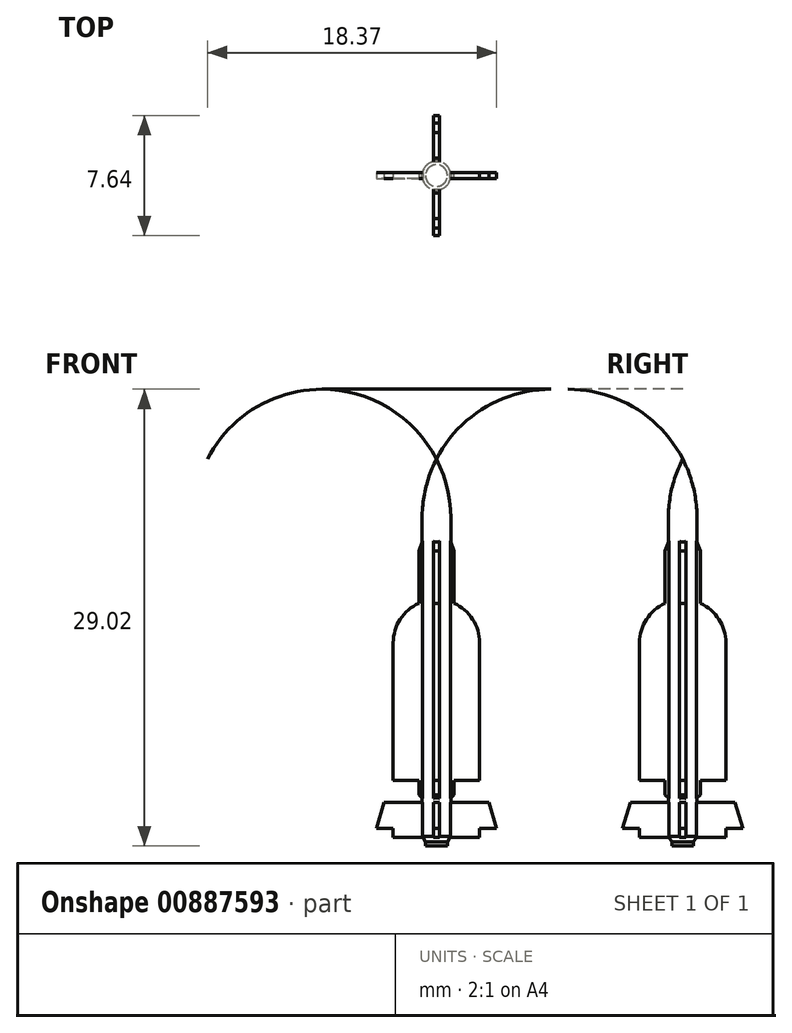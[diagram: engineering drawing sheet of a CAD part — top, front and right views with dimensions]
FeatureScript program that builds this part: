
annotation { "Feature Type Name" : "Feature", "Feature Type Description" : "" }
export const myFeature = defineFeature(function(context is Context, id is Id, definition is map)
    precondition{}
    {
        {
            var Q0;
            Q0=qCreatedBy(makeId("Front.planeOp"),FACE);
            var sketch = newSketch(context, id + "F0", { "sketchPlane" : qUnion([Q0])});
            skLineSegment(sketch, "E0", {"start": v(0, 0) * mm, "end": v(0, 24.58) * mm});
            skLineSegment(sketch, "E1", {"start": v(0.9, 20.83) * mm, "end": v(0.9, 0) * mm});
            skLineSegment(sketch, "E2", {"start": v(0.9, 0) * mm, "end": v(0, 0) * mm});
            skArc(sketch, "E3", {"start": v(0.9, 20.83) * mm, "mid": v(0.68, 22.76) * mm, "end": v(0, 24.58) * mm});
            skLineSegment(sketch, "E4", {"start": v(0.7, 0) * mm, "end": v(0.7, 0.28) * mm});
            skLineSegment(sketch, "E5", {"start": v(0.7, 0.28) * mm, "end": v(0.9, 0.63) * mm});
            skSolve(sketch);
        }
        {
            var Q0;
            {var subQ0=sQuery(id+"F0.wireOp",EDGE,"mrwio9nY-PsAZ-Zbfy-NhIU-sYq0QVbgGXAG");Q0=makeQuery(id+"F0.imprint","IMPRINT",FACE,{"disambiguationData":[TD([[makeQuery(id+"F0.imprint","IMPRINT",EDGE,{"derivedFrom":subQ0}),-1.0]])]});}
            var Q1;
            Q1=makeQuery(id+"F0.imprint","IMPRINT",FACE,{"disambiguationData":[TD([[makeQuery(id+"F0.imprint","IMPRINT",EDGE,{"derivedFrom":sQuery(id+"F0.wireOp",EDGE,"rEedh4zr-IGRr-Hqzj-sDLB-QnI7VE1V64O6.bottom")}),-1.0]])]});
            var Q2;
            Q2=makeQuery(id+"F0.imprint","IMPRINT",FACE,{"disambiguationData":[TD([[makeQuery(id+"F0.imprint","IMPRINT",EDGE,{"derivedFrom":sQuery(id+"F0.wireOp",EDGE,"E0")}),-1.0]])]});
            var Q3;
            Q3=makeQuery(id+"F0.imprint","IMPRINT",FACE,{"disambiguationData":[TD([[makeQuery(id+"F0.imprint","IMPRINT",EDGE,{"derivedFrom":sQuery(id+"F0.wireOp",EDGE,"p5wuz8j9-3HT4-kWwn-DjtP-lJmqTNSXSBJY.bottom")}),-1.0]])]});
            var Q4;
            Q4=sQuery(id+"F0.wireOp",EDGE,"E0");
            revolve(context, id + "F1", {"surfaceOperationType" : NewSurfaceOperationType.NEW, "entities" : qUnion([Q0, Q1, Q2, Q3]), "axis" : qUnion([Q4]), "revolveType" : RevolveType.FULL});
        }
        {
            var Q0;
            Q0=qCreatedBy(makeId("Front.planeOp"),FACE);
            var sketch = newSketch(context, id + "F2", { "sketchPlane" : qUnion([Q0])});
            skLineSegment(sketch, "E6", {"start": v(0, 0) * mm, "end": v(0, 21.8) * mm});
            skLineSegment(sketch, "E7", {"start": v(1.12, 3.26) * mm, "end": v(0.8, 2.95) * mm});
            skLineSegment(sketch, "E8", {"start": v(0.8, 2.78) * mm, "end": v(3.33, 2.78) * mm});
            skLineSegment(sketch, "E9", {"start": v(0.9, 0) * mm, "end": v(0.9, 32.87) * mm, "construction": true});
            skPoint(sketch, "E10", {"position": v(0.9, 3.06) * mm});
            skLineSegment(sketch, "E11", {"start": v(2.74, 0.56) * mm, "end": v(0, 0.56) * mm});
            skLineSegment(sketch, "E12", {"start": v(1.12, 3.26) * mm, "end": v(1.12, 4.17) * mm});
            skLineSegment(sketch, "E13.0", {"start": v(0.9, 0.63) * mm, "end": v(-0.9, 0.63) * mm});
            skLineSegment(sketch, "E14", {"start": v(2.74, 0.56) * mm, "end": v(2.74, 1.11) * mm});
            skLineSegment(sketch, "E15", {"start": v(2.74, 1.11) * mm, "end": v(3.82, 1.11) * mm});
            skLineSegment(sketch, "E16", {"start": v(3.82, 1.11) * mm, "end": v(3.33, 2.78) * mm});
            skLineSegment(sketch, "E17", {"start": v(0.8, 2.95) * mm, "end": v(0.8, 2.78) * mm});
            skLineSegment(sketch, "E18", {"start": v(1.12, 4.17) * mm, "end": v(2.74, 4.17) * mm});
            skLineSegment(sketch, "E19", {"start": v(2.74, 4.17) * mm, "end": v(2.74, 12.92) * mm});
            skArc(sketch, "E20", {"start": v(2.74, 12.92) * mm, "mid": v(2.24, 14.5) * mm, "end": v(0.9, 15.5) * mm});
            skPoint(sketch, "E21", {"position": v(0.9, 15.5) * mm});
            skLineSegment(sketch, "E22", {"start": v(1.12, 15.42) * mm, "end": v(1.12, 18.73) * mm});
            skLineSegment(sketch, "E23", {"start": v(1.12, 18.73) * mm, "end": v(0, 21.8) * mm});
            skPoint(sketch, "E24", {"position": v(0.9, 19.3) * mm});
            skSolve(sketch);
        }
        {
            var Q0;
            Q0=qSketchRegion(id+"F2",true);
            extrude(context, id + "F3", {"entities" : qUnion([Q0]), "operationType" : NewBodyOperationType.ADD, "depth" : .4 * mm, "offsetDistance" : 25 * mm, "symmetric" : true});
        }
        {
            var Q0;
            Q0=makeQuery(id+"F1.opRevolve","SWEPT_BODY",BODY,{"disambiguationData":[OSD([sQuery(id+"F0.wireOp",EDGE,"E0"),sQuery(id+"F0.wireOp",EDGE,"E1"),sQuery(id+"F0.wireOp",EDGE,"E2"),sQuery(id+"F0.wireOp",EDGE,"2EiOItwe-9FNA-eY8p-DkXH-AMy5AHyUmzZA"),sQuery(id+"F0.wireOp",EDGE,"E3")])]});
            var Q1;
            Q1=makeQuery(id+"F1.opRevolve","SWEPT_FACE",FACE,{"disambiguationData":[OSD([sQuery(id+"F0.wireOp",EDGE,"E1")])]});
            circularPattern(context, id + "F4", {"operationType" : NewBodyOperationType.ADD, "entities" : qUnion([Q0]), "axis" : qUnion([Q1]), "angle" : 360 * degree, "instanceCount" : 4, "equalSpace" : true, "computeTransformsWithoutBuiltin" : true});
        }
    });
